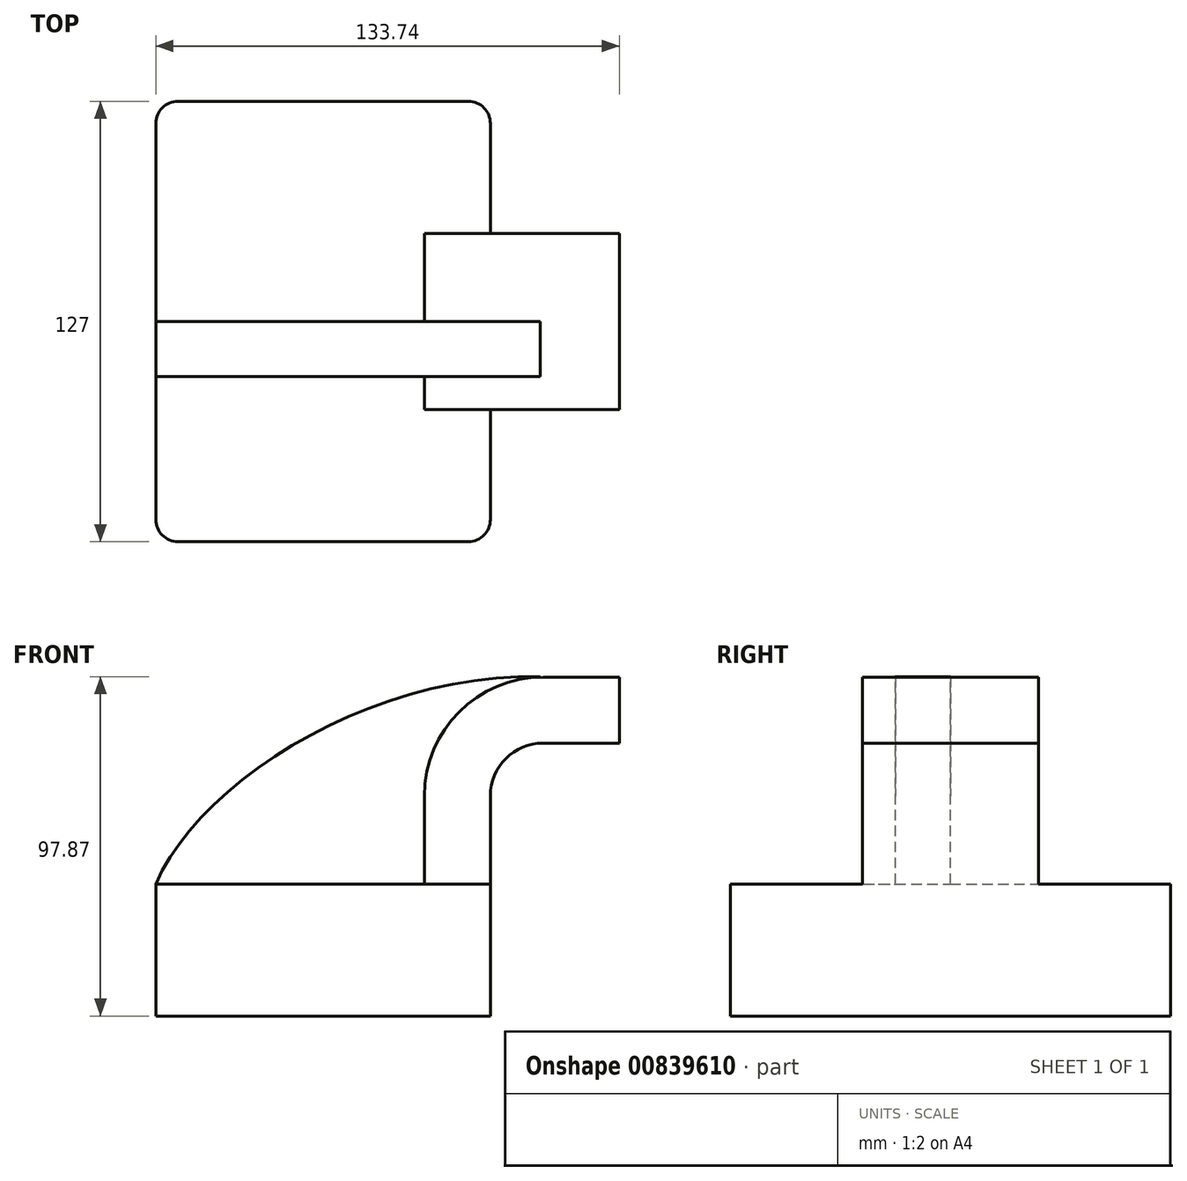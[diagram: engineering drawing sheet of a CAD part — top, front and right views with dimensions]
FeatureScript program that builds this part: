
annotation { "Feature Type Name" : "Feature", "Feature Type Description" : "" }
export const myFeature = defineFeature(function(context is Context, id is Id, definition is map)
    precondition{}
    {
        {
            var Q0;
            Q0=qCreatedBy(makeId("Front.planeOp"),FACE);
            var sketch = newSketch(context, id + "F0", { "sketchPlane" : qUnion([Q0])});
            skLineSegment(sketch, "E0.bottom", {"start": v(-48.26, 19.05) * mm, "end": v(48.26, 19.05) * mm});
            skLineSegment(sketch, "E0.top", {"start": v(-48.26, -19.05) * mm, "end": v(48.26, -19.05) * mm});
            skLineSegment(sketch, "E0.left", {"start": v(-48.26, 19.05) * mm, "end": v(-48.26, -19.05) * mm});
            skLineSegment(sketch, "E0.right", {"start": v(48.26, 19.05) * mm, "end": v(48.26, -19.05) * mm});
            skPoint(sketch, "E0.middle", {"position": v(0, 0) * mm});
            skLineSegment(sketch, "E1", {"start": v(48.26, 19.05) * mm, "end": v(48.26, 44.45) * mm});
            skArc(sketch, "E2", {"start": v(48.26, 44.45) * mm, "mid": v(52.72, 55.23) * mm, "end": v(63.5, 59.7) * mm});
            skLineSegment(sketch, "E3", {"start": v(63.5, 59.7) * mm, "end": v(85.48, 59.7) * mm});
            skLineSegment(sketch, "E4.bottom", {"start": v(62.62, 82.55) * mm, "end": v(108.34, 82.55) * mm});
            skLineSegment(sketch, "E4.top", {"start": v(62.62, 52.07) * mm, "end": v(108.34, 52.07) * mm});
            skLineSegment(sketch, "E4.left", {"start": v(62.62, 82.55) * mm, "end": v(62.62, 52.07) * mm});
            skLineSegment(sketch, "E4.right", {"start": v(108.34, 82.55) * mm, "end": v(108.34, 52.07) * mm});
            skPoint(sketch, "E4.middle", {"position": v(85.48, 67.31) * mm});
            skLineSegment(sketch, "E5.0", {"start": v(63.5, 78.74) * mm, "end": v(85.48, 78.74) * mm});
            skArc(sketch, "E5.1", {"start": v(29.2, 44.45) * mm, "mid": v(39.25, 68.7) * mm, "end": v(63.5, 78.74) * mm});
            skLineSegment(sketch, "E5.2", {"start": v(29.2, 19.05) * mm, "end": v(29.2, 44.45) * mm});
            skLineSegment(sketch, "E6", {"start": v(85.48, 52.07) * mm, "end": v(85.48, 82.55) * mm});
            skFitSpline(sketch, "E7", {"points": [v(-48.26, 19.05) * mm, v(63.5, 78.74) * mm], "startDerivative": vector(37.72, 88.5) * mm, "endDerivative": vector(146.51, -5.7) * mm});
            skSolve(sketch);
        }
        {
            var Q0;
            Q0=makeQuery(id+"F0.imprint","IMPRINT",FACE,{"disambiguationData":[TD([[makeQuery(id+"F0.imprint","IMPRINT",EDGE,{"derivedFrom":sQuery(id+"F0.wireOp",EDGE,"E0.top")}),1.0]])]});
            extrude(context, id + "F1", {"entities" : qUnion([Q0]), "endBound" : BoundingType.SYMMETRIC, "depth" : 127 * mm, "offsetDistance" : 25.4 * mm});
        }
        {
            var Q0;
            {var subQ5=sQuery(id+"F0.wireOp",EDGE,"E1");Q0=makeQuery(id+"F0.imprint","IMPRINT",FACE,{"disambiguationData":[TD([[makeQuery(id+"F0.imprint","IMPRINT",EDGE,{"derivedFrom":subQ5}),1.0]])]});}
            var Q1;
            {var subQ6=sQuery(id+"F0.wireOp",EDGE,"E3");Q1=makeQuery(id+"F0.imprint","IMPRINT",FACE,{"disambiguationData":[TD([[makeQuery(id+"F0.imprint","IMPRINT",EDGE,{"derivedFrom":subQ6}),1.0]])]});}
            extrude(context, id + "F2", {"entities" : qUnion([Q0, Q1]), "operationType" : NewBodyOperationType.ADD, "endBound" : BoundingType.SYMMETRIC, "depth" : 50.8 * mm, "offsetDistance" : 25.4 * mm});
        }
        {
            var Q0;
            {var subQ0=sQuery(id+"F0.wireOp",EDGE,"E5.2");Q0=makeQuery(id+"F0.imprint","IMPRINT",FACE,{"disambiguationData":[TD([[makeQuery(id+"F0.imprint","IMPRINT",EDGE,{"derivedFrom":subQ0}),1.0]])]});}
            extrude(context, id + "F3", {"entities" : qUnion([Q0]), "operationType" : NewBodyOperationType.ADD, "depth" : 15.88 * mm, "offsetDistance" : 25.4 * mm});
        }
        {
            var Q0;
            Q0=makeQuery(id+"F1.opExtrude","CAP_EDGE",EDGE,{"disambiguationData":[OSD([sQuery(id+"F0.wireOp",EDGE,"E0.right")])],"isStart":false});
            var Q1;
            Q1=makeQuery(id+"F1.opExtrude","CAP_EDGE",EDGE,{"disambiguationData":[OSD([sQuery(id+"F0.wireOp",EDGE,"E0.left")])],"isStart":false});
            var Q2;
            Q2=makeQuery(id+"F1.opExtrude","CAP_EDGE",EDGE,{"disambiguationData":[OSD([sQuery(id+"F0.wireOp",EDGE,"E0.right")])],"isStart":true});
            var Q3;
            Q3=makeQuery(id+"F1.opExtrude","CAP_EDGE",EDGE,{"disambiguationData":[OSD([sQuery(id+"F0.wireOp",EDGE,"E0.left")])],"isStart":true});
            fillet(context, id + "F4", {"entities" : qUnion([Q0, Q1, Q2, Q3]), "radius" : 6.35 * mm, "tangentPropagation" : true, "allowEdgeOverflow" : false});
        }
    });
